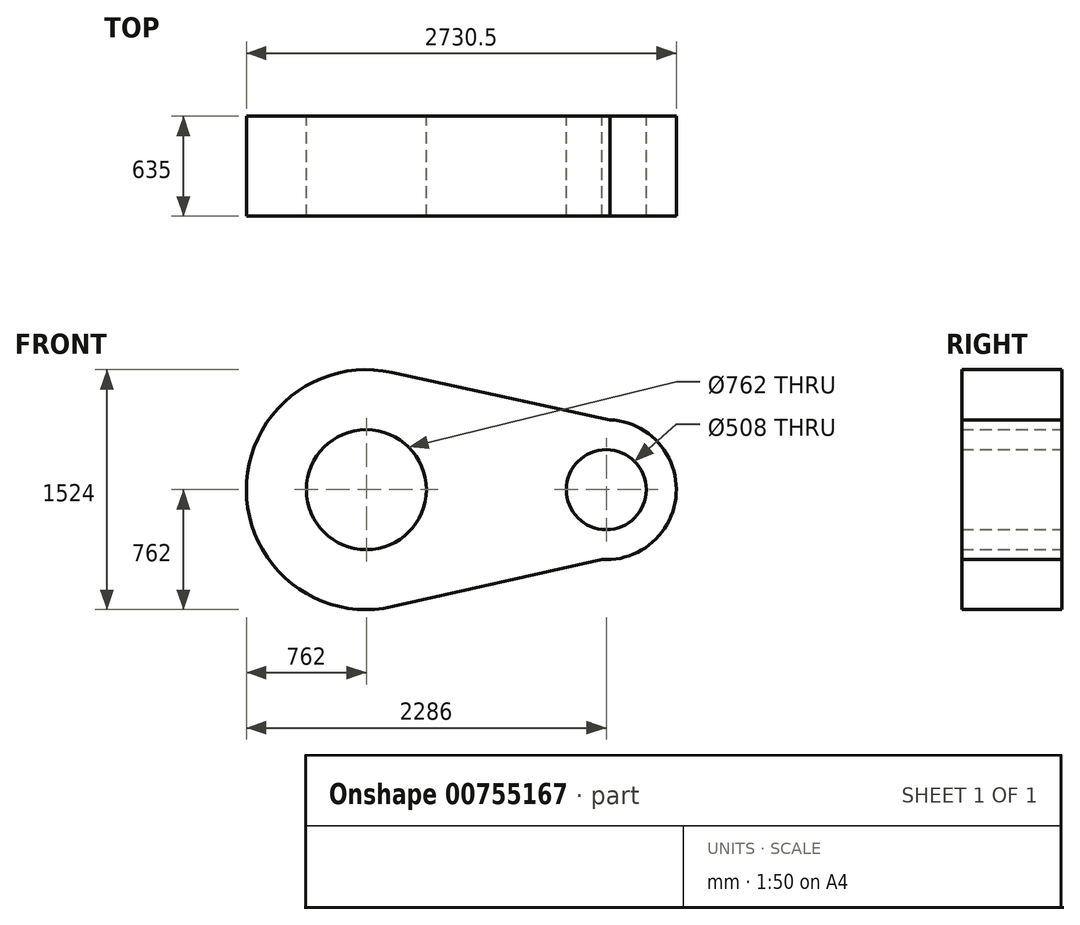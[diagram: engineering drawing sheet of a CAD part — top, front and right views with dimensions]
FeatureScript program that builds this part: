
annotation { "Feature Type Name" : "Feature", "Feature Type Description" : "" }
export const myFeature = defineFeature(function(context is Context, id is Id, definition is map)
    precondition{}
    {
        {
            var Q0;
            Q0=qCreatedBy(makeId("Front.planeOp"),FACE);
            var sketch = newSketch(context, id + "F0", { "sketchPlane" : qUnion([Q0])});
            skCircle(sketch, "E0", {"center": v(0, 0) * mm, "radius": 762 * mm});
            skCircle(sketch, "E1", {"center": v(1524, 0) * mm, "radius": 444.5 * mm});
            skLineSegment(sketch, "E2", {"start": v(161.6, 744.67) * mm, "end": v(1547.82, 443.86) * mm});
            skLineSegment(sketch, "E3", {"start": v(167.76, -743.3) * mm, "end": v(1495.66, -443.6) * mm});
            skCircle(sketch, "E4", {"center": v(0, 0) * mm, "radius": 381 * mm});
            skCircle(sketch, "E5", {"center": v(1524, 0) * mm, "radius": 254 * mm});
            skSolve(sketch);
        }
        {
            var Q0;
            Q0=makeQuery(id+"F0.imprint","IMPRINT",FACE,{"disambiguationData":[TD([[makeQuery(id+"F0.imprint","IMPRINT",EDGE,{"derivedFrom":sQuery(id+"F0.wireOp",EDGE,"E4")}),-1.0]])]});
            var Q1;
            {var subQ0=sQuery(id+"F0.wireOp",EDGE,"E2");Q1=makeQuery(id+"F0.imprint","IMPRINT",FACE,{"disambiguationData":[TD([[makeQuery(id+"F0.imprint","IMPRINT",EDGE,{"derivedFrom":subQ0}),-1.0]])]});}
            var Q2;
            Q2=makeQuery(id+"F0.imprint","IMPRINT",FACE,{"disambiguationData":[TD([[makeQuery(id+"F0.imprint","IMPRINT",EDGE,{"derivedFrom":sQuery(id+"F0.wireOp",EDGE,"E5")}),-1.0]])]});
            extrude(context, id + "F1", {"entities" : qUnion([Q0, Q1, Q2]), "depth" : 635 * mm, "offsetDistance" : 25.4 * mm});
        }
    });
